# Revit family: BLAUBERG-CIVIC_EC_LB300
name_source: partatom
category: Mechanical Equipment
units: mm (PartAtom-declared; Revit-internal decimal feet)

## family parameters
Always vertical = Yes
Classification = None
Cut with Voids When Loaded = No
OmniClass Number = 23.75.35.14
OmniClass Title = Air Handling Units
Part Type = Normal
Room Calculation Point = No
Round Connector Dimension = Use Diameter
Shared = No
Work Plane-Based = No

## types (8) — shared parameters
Casing Material = Painted Steel White
D1 = 197 mm
Description = Single-room heat recovery air handling unit
Drain Connection Diameter = 8 mm  [stored 0.0262467 ft]
Duct Connection Diameter = 200 mm  [stored 0.656168 ft]
Extract Air Filter = G4x2
Family Version = 1.0
Grid Material = Grid Cross
H = 1762 mm  [stored 5.78084 ft]
H1 = 1476 mm
H2 = 286 mm
Hb = 100 mm  [stored 0.328084 ft]
Hc = 1662 mm  [stored 5.45276 ft]
Heat Exchanger Type = counter-flow
Ht = 13 mm
L = 470 mm  [stored 1.54199 ft]
L1 = 520 mm  [stored 1.70604 ft]
Load Classification = HVAC
Maintenance Zone Front Depth = 600 mm
Maintenance Zone Material = Maintenance Zone
Maintenance Zone Side Depth = 350 mm  [stored 1.14829 ft]
Manufacturer = Blauberg
Maximum Air Flow = 320 m³/h
Maximum Unit Current Without Electric Heater = 1 A
Maximum Unit Power Without Electric Heater = 125 W
Number of Poles = 1
Power Factor = 1
RPM (min-1) = 2150
SEC Class = A
Sound Pressure Level at 1 m (dBA) = 31
Sound Pressure Level at 3 m (dBA) = 21
Supply Air Filter = G4+F8
Transported Air Temperature (°C) = –25 …+40
URL = https://blaubergventilatoren.de
Voltage = 230 V
W = 620 mm  [stored 2.03412 ft]
W1 = 230 mm  [stored 0.754593 ft]
W2 = 195 mm  [stored 0.639764 ft]
dL = 5 mm  [stored 0.0164042 ft]
dW = 5 mm  [stored 0.0164042 ft]
elConBack = 90 mm  [stored 0.295276 ft]
elConSide = 170 mm  [stored 0.557743 ft]
ofH = 125 mm  [stored 0.410105 ft]
ofLeft = 50 mm  [stored 0.164042 ft]
ofLeftCenter = 310 mm  [stored 1.01706 ft]
ofRight = 50 mm  [stored 0.164042 ft]
ofRightCenter = 310 mm  [stored 1.01706 ft]
ofTopOfCenter = 125 mm  [stored 0.410105 ft]
ofW = 520 mm  [stored 1.70604 ft]
osBack = 70 mm  [stored 0.229659 ft]
osH = 240 mm  [stored 0.787402 ft]
osTopOfCenter = 330 mm
osW = 310 mm  [stored 1.01706 ft]

## per-type parameters (varying)
| type | Current | Heat Exchanger Material | Heat recovery efficiency (%) | Maximum Unit Current With Electric Heater | Power | Preheater power | Reheater power | Type Comments | Weight |
| CIVIC EC LB 300 S21 | 1 A | polystyrene | 78..92 | 1 A | 125 W | 0 W | 0 W | Single-room heat recovery air handling unit CIVIC EC LB 300 S21 | 138.00 kg |
| CIVIC EC LB 300 S14 | 1 A | polystyrene | 78..92 | 1 A | 125 W | 0 W | 0 W | Single-room heat recovery air handling unit CIVIC EC LB 300 S14 | 138.00 kg |
| CIVIC EC LBE 300 S21 | 7 A | polystyrene | 78..92 | 7 A | 1525 W | 1400 W | 0 W | Single-room heat recovery air handling unit CIVIC EC LBE 300 S21 | 139.00 kg |
| CIVIC EC LBE2 300 S21 | 13 A | polystyrene | 78..92 | 13 A | 2925 W | 1400 W | 1400 W | Single-room heat recovery air handling unit CIVIC EC LBE2 300 S21 | 140.00 kg |
| CIVIC EC LB 300-E S21 | 1 A | enthalpy | 73..89 | 1 A | 125 W | 0 W | 0 W | Single-room heat recovery air handling unit CIVIC EC LB 300-E S21 | 136.00 kg |
| CIVIC EC LB 300-E S14 | 1 A | enthalpy | 73..89 | 1 A | 125 W | 0 W | 0 W | Single-room heat recovery air handling unit CIVIC EC LB 300-E S14 | 136.00 kg |
| CIVIC EC LBE 300-E S21 | 7 A | enthalpy | 73..89 | 7 A | 1525 W | 1400 W | 0 W | Single-room heat recovery air handling unit CIVIC EC LBE 300-E S21 | 137.00 kg |
| CIVIC EC LBE2 300-E S21 | 13 A | enthalpy | 73..89 | 13 A | 2925 W | 1400 W | 1400 W | Single-room heat recovery air handling unit CIVIC EC LBE2 300-E S21 | 138.00 kg |

note: column(s) folded — value = type name in every type: Model

note: [stored X ft] marks values corroborated as IEEE doubles in the binary element streams (Revit-internal decimal feet)

## geometry (parser evidence)
native form markers: Sweep x9
no freeform markers — native parametric forms only
